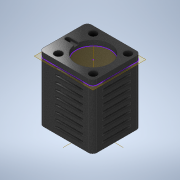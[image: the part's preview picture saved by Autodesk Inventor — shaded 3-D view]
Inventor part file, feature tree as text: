
AUTODESK INVENTOR PART (.ipt)
format: ipt  version: 2021.1 (Build 251245000, 245)  size: 284,672 bytes
history: native  units: in
note: dims shown in document units (in); Inventor stores cm internally (conversion verified against a paired STEP export)
features: sketch x6, extrude x6, projected_geometry x4, revolve x1, plane x1, pattern_linear x1
ambient origin geometry x8: Origin, YZ Plane, XZ Plane, XY Plane, X Axis, Y Axis, Z Axis, Center Point
bodies: Solid1 (feature_tree)
feature tree (19):
  sketch  "Sketch1"  dims[d0=5.0in d1=4.5in]
  extrude  "Extrusion1"  Depth=4.5in
  extrude  "Extrusion2"  Depth=0.4in
  extrude  "Extrusion3"  Depth=3.2in
  sketch  "Sketch3"  dims[d4=6.2in d5=0.0in d6=3.2in]
  extrude  "Extrusion4"  Depth=4.6in
  extrude  "Extrusion5"  Depth=0.7in
  revolve  "Revolution1"  [1 undecoded]
  plane  "Work Plane1"
  sketch  "Sketch5"  dims[d10=45.0deg d11=0.7in]
  extrude  "Extrusion6"  Depth=0.4in
  pattern_linear  "Rectangular Pattern1"  Spacing1=2.4in  [1 undecoded]
  sketch  "Sketch2"  dims[d2=2.2in d3=0.4in]
  sketch  "Sketch4"  dims[d7=6.2in d8=0.0in d9=4.6in]
  projected_geometry  "Projected Loop1"
  sketch  "Sketch6"  dims[d12=1.5748in d14=360.0deg d16=0.0in d17=0.0in d18=0.4in d19=2.4in d20=0.4in d21=0.0in d22=0.0in d23=0.2in d24=0.0in d25=3.6in d26=0.2in d27=2.0in d28=90.0deg d29=-0.5in d32=4.8in d33=2.0in d34=4.8in d35=2.0in d36=4.8in d37=2.0in d38=0.2in d39=0.0in d40=3.5433in d42=0.6in]
  projected_geometry  "Projected Loop2"
  projected_geometry  "Project Cut Edges1"
  projected_geometry  "Project Cut Edges4"
note: 2 required parameter values undecoded (feature->parameter linkage not recoverable at this tier; creation-order binding heuristic only, values carry confidence <= 0.55)